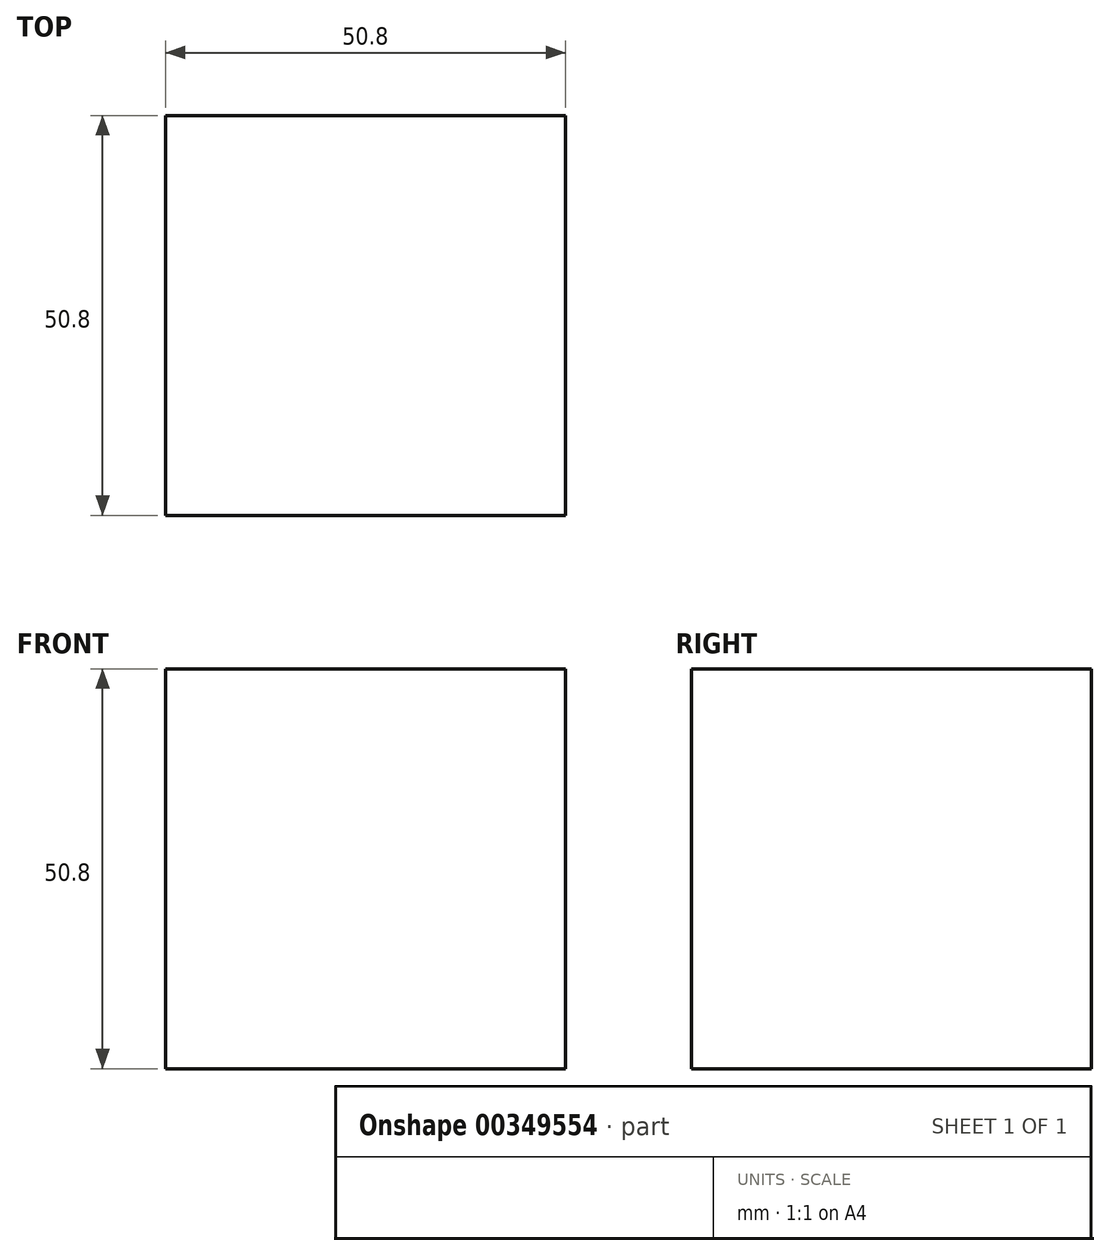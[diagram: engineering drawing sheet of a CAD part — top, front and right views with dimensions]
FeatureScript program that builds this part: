
annotation { "Feature Type Name" : "Feature", "Feature Type Description" : "" }
export const myFeature = defineFeature(function(context is Context, id is Id, definition is map)
    precondition{}
    {
        {
            var Q0;
            Q0=qCreatedBy(makeId("Top.planeOp"),FACE);
            var sketch = newSketch(context, id + "F0", { "sketchPlane" : qUnion([Q0])});
            skLineSegment(sketch, "E0.bottom", {"start": v(-25.4, -25.4) * mm, "end": v(25.4, -25.4) * mm});
            skLineSegment(sketch, "E0.top", {"start": v(-25.4, 25.4) * mm, "end": v(25.4, 25.4) * mm});
            skLineSegment(sketch, "E0.left", {"start": v(-25.4, -25.4) * mm, "end": v(-25.4, 25.4) * mm});
            skLineSegment(sketch, "E0.right", {"start": v(25.4, -25.4) * mm, "end": v(25.4, 25.4) * mm});
            skPoint(sketch, "E0.middle", {"position": v(0, 0) * mm});
            skSolve(sketch);
        }
        {
            var Q0;
            Q0=makeQuery(id+"F0.imprint","IMPRINT",FACE,{"disambiguationData":[TD([[makeQuery(id+"F0.imprint","IMPRINT",EDGE,{"derivedFrom":sQuery(id+"F0.wireOp",EDGE,"E0.bottom")}),1.0]])]});
            extrude(context, id + "F1", {"entities" : qUnion([Q0]), "depth" : 50.8 * mm});
        }
    });
